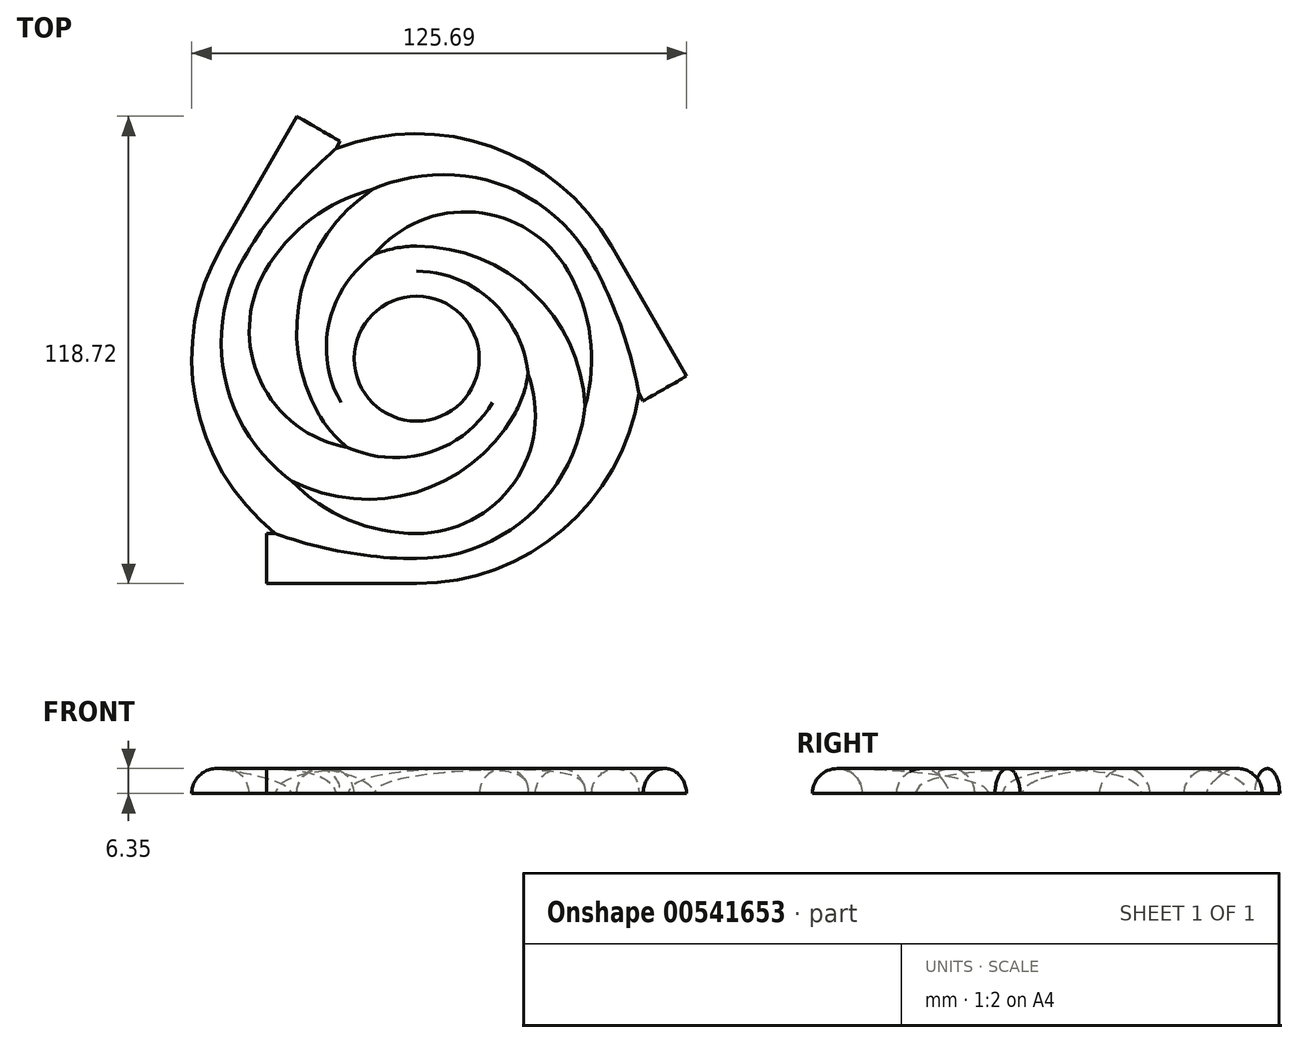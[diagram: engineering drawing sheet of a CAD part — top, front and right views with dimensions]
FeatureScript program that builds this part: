
annotation { "Feature Type Name" : "Feature", "Feature Type Description" : "" }
export const myFeature = defineFeature(function(context is Context, id is Id, definition is map)
    precondition{}
    {
        {
            var Q0;
            Q0=qCreatedBy(makeId("Top.planeOp"),FACE);
            var sketch = newSketch(context, id + "F0", { "sketchPlane" : qUnion([Q0])});
            skCircle(sketch, "E0", {"center": v(0, 0) * mm, "radius": 22.23 * mm});
            skCircle(sketch, "E1", {"center": v(0, 0) * mm, "radius": 50.8 * mm});
            skArc(sketch, "E2", {"start": v(44, 25.4) * mm, "mid": v(-5.88, 38.76) * mm, "end": v(-19.25, -11.11) * mm});
            skArc(sketch, "E3", {"start": v(-44, 25.4) * mm, "mid": v(-30.63, -24.48) * mm, "end": v(19.25, -11.11) * mm});
            skArc(sketch, "E4", {"start": v(0, -50.8) * mm, "mid": v(36.51, -14.29) * mm, "end": v(0, 22.23) * mm});
            skLineSegment(sketch, "E5", {"start": v(0, 0) * mm, "end": v(0, 22.22) * mm, "construction": true});
            skLineSegment(sketch, "E6", {"start": v(0, 0) * mm, "end": v(19.25, -11.11) * mm, "construction": true});
            skLineSegment(sketch, "E7", {"start": v(0, 0) * mm, "end": v(-19.25, -11.11) * mm, "construction": true});
            skLineSegment(sketch, "E8", {"start": v(0, -50.8) * mm, "end": v(-38.1, -50.8) * mm});
            skLineSegment(sketch, "E9", {"start": v(-44, 25.4) * mm, "end": v(-24.94, 58.4) * mm});
            skLineSegment(sketch, "E10", {"start": v(44, 25.4) * mm, "end": v(63.04, -7.6) * mm});
            skPoint(sketch, "E11", {"position": v(50.8, 0) * mm});
            skPoint(sketch, "E12", {"position": v(22.23, 0) * mm});
            skSolve(sketch);
        }
        {
            var Q0;
            Q0=sQuery(id+"F0.wireOp",EDGE,"E9");
            var Q1;
            Q1=sQuery(id+"F0.wireOp",VERTEX,"E3.start");
            cPlane(context, id + "F1", {"entities" : qUnion([Q0, Q1]), "cplaneType" : CPlaneType.LINE_POINT, "offset" : 25.4 * mm, "width" : 152.4 * mm, "height" : 152.4 * mm});
        }
        {
            var Q0;
            Q0=sQuery(id+"F0.wireOp",EDGE,"E10");
            var Q1;
            Q1=sQuery(id+"F0.wireOp",VERTEX,"E2.start");
            cPlane(context, id + "F2", {"entities" : qUnion([Q0, Q1]), "cplaneType" : CPlaneType.LINE_POINT, "offset" : 25.4 * mm, "width" : 152.4 * mm, "height" : 152.4 * mm});
        }
        {
            var Q0;
            Q0=qCreatedBy(id+"F2.planeOp",FACE);
            var sketch = newSketch(context, id + "F3", { "sketchPlane" : qUnion([Q0])});
            skArc(sketch, "E13", {"start": v(57.15, 0) * mm, "mid": v(50.8, 6.35) * mm, "end": v(44.45, 0) * mm});
            skLineSegment(sketch, "E14", {"start": v(44.45, 0) * mm, "end": v(57.15, 0) * mm});
            skSolve(sketch);
        }
        {
            var Q0;
            Q0=qCreatedBy(id+"F1.planeOp",FACE);
            var sketch = newSketch(context, id + "F4", { "sketchPlane" : qUnion([Q0])});
            skArc(sketch, "E15", {"start": v(57.15, 0) * mm, "mid": v(50.8, 6.35) * mm, "end": v(44.45, 0) * mm});
            skLineSegment(sketch, "E16", {"start": v(57.15, 0) * mm, "end": v(44.45, 0) * mm});
            skSolve(sketch);
        }
        {
            var Q0;
            Q0=qCreatedBy(makeId("Right.planeOp"),FACE);
            var sketch = newSketch(context, id + "F5", { "sketchPlane" : qUnion([Q0])});
            skArc(sketch, "E17", {"start": v(-44.45, 0) * mm, "mid": v(-50.8, 6.35) * mm, "end": v(-57.15, 0) * mm});
            skLineSegment(sketch, "E18", {"start": v(-57.15, 0) * mm, "end": v(-44.45, 0) * mm});
            skSolve(sketch);
        }
        {
            var Q0;
            Q0=qCreatedBy(makeId("Front.planeOp"),FACE);
            var sketch = newSketch(context, id + "F6", { "sketchPlane" : qUnion([Q0])});
            skArc(sketch, "E19", {"start": v(57.15, 0) * mm, "mid": v(50.8, 6.35) * mm, "end": v(44.45, 0) * mm});
            skLineSegment(sketch, "E20", {"start": v(44.45, 0) * mm, "end": v(57.15, 0) * mm});
            skArc(sketch, "E21", {"start": v(28.58, 0) * mm, "mid": v(22.23, 6.35) * mm, "end": v(15.88, 0) * mm});
            skLineSegment(sketch, "E22", {"start": v(15.88, 0) * mm, "end": v(28.58, 0) * mm});
            skSolve(sketch);
        }
        {
            var Q0;
            Q0=makeQuery(id+"F5.imprint","IMPRINT",FACE,{"disambiguationData":[TD([[makeQuery(id+"F5.imprint","IMPRINT",EDGE,{"derivedFrom":sQuery(id+"F5.wireOp",EDGE,"E17")}),1.0]])]});
            var Q1;
            Q1=sQuery(id+"F0.wireOp",EDGE,"E4");
            sweep(context, id + "F7", {"profiles" : qUnion([Q0]), "path" : qUnion([Q1])});
        }
        {
            var Q0;
            Q0=makeQuery(id+"F3.imprint","IMPRINT",FACE,{"disambiguationData":[TD([[makeQuery(id+"F3.imprint","IMPRINT",EDGE,{"derivedFrom":sQuery(id+"F3.wireOp",EDGE,"E13")}),1.0]])]});
            var Q1;
            Q1=sQuery(id+"F0.wireOp",EDGE,"E2");
            sweep(context, id + "F8", {"operationType" : NewBodyOperationType.ADD, "profiles" : qUnion([Q0]), "path" : qUnion([Q1])});
        }
        {
            var Q0;
            Q0=makeQuery(id+"F4.imprint","IMPRINT",FACE,{"disambiguationData":[TD([[makeQuery(id+"F4.imprint","IMPRINT",EDGE,{"derivedFrom":sQuery(id+"F4.wireOp",EDGE,"E15")}),1.0]])]});
            var Q1;
            Q1=sQuery(id+"F0.wireOp",EDGE,"E3");
            sweep(context, id + "F9", {"operationType" : NewBodyOperationType.ADD, "profiles" : qUnion([Q0]), "path" : qUnion([Q1])});
        }
        {
            var Q0;
            Q0=makeQuery(id+"F6.imprint","IMPRINT",FACE,{"disambiguationData":[TD([[makeQuery(id+"F6.imprint","IMPRINT",EDGE,{"derivedFrom":sQuery(id+"F6.wireOp",EDGE,"E19")}),1.0]])]});
            var Q1;
            Q1=sQuery(id+"F0.wireOp",EDGE,"E1");
            sweep(context, id + "F10", {"operationType" : NewBodyOperationType.ADD, "profiles" : qUnion([Q0]), "path" : qUnion([Q1])});
        }
        {
            var Q0;
            Q0=makeQuery(id+"F6.imprint","IMPRINT",FACE,{"disambiguationData":[TD([[makeQuery(id+"F6.imprint","IMPRINT",EDGE,{"derivedFrom":sQuery(id+"F6.wireOp",EDGE,"E21")}),1.0]])]});
            var Q1;
            Q1=sQuery(id+"F0.wireOp",EDGE,"E0");
            sweep(context, id + "F11", {"operationType" : NewBodyOperationType.ADD, "profiles" : qUnion([Q0]), "path" : qUnion([Q1])});
        }
        {
            var Q0;
            Q0=makeQuery(id+"F3.imprint","IMPRINT",FACE,{"disambiguationData":[TD([[makeQuery(id+"F3.imprint","IMPRINT",EDGE,{"derivedFrom":sQuery(id+"F3.wireOp",EDGE,"E13")}),1.0]])]});
            var Q1;
            Q1=sQuery(id+"F0.wireOp",EDGE,"E10");
            sweep(context, id + "F12", {"operationType" : NewBodyOperationType.ADD, "profiles" : qUnion([Q0]), "path" : qUnion([Q1])});
        }
        {
            var Q0;
            Q0=makeQuery(id+"F4.imprint","IMPRINT",FACE,{"disambiguationData":[TD([[makeQuery(id+"F4.imprint","IMPRINT",EDGE,{"derivedFrom":sQuery(id+"F4.wireOp",EDGE,"E15")}),1.0]])]});
            var Q1;
            Q1=sQuery(id+"F0.wireOp",EDGE,"E9");
            sweep(context, id + "F13", {"operationType" : NewBodyOperationType.ADD, "profiles" : qUnion([Q0]), "path" : qUnion([Q1])});
        }
        {
            var Q0;
            Q0=makeQuery(id+"F5.imprint","IMPRINT",FACE,{"disambiguationData":[TD([[makeQuery(id+"F5.imprint","IMPRINT",EDGE,{"derivedFrom":sQuery(id+"F5.wireOp",EDGE,"E17")}),1.0]])]});
            var Q1;
            Q1=sQuery(id+"F0.wireOp",EDGE,"E8");
            sweep(context, id + "F14", {"operationType" : NewBodyOperationType.ADD, "profiles" : qUnion([Q0]), "path" : qUnion([Q1])});
        }
    });
